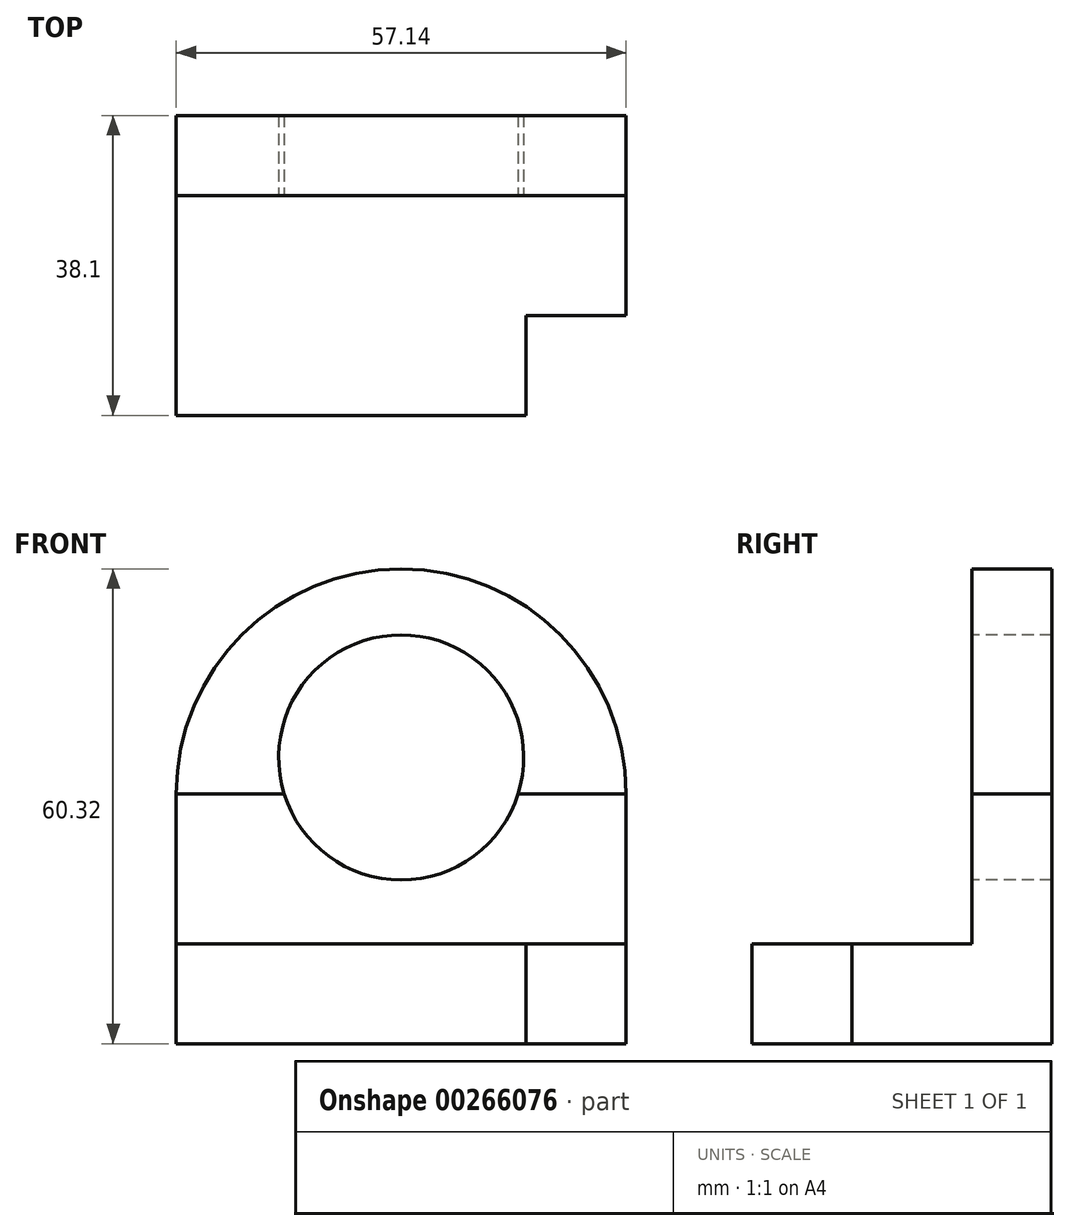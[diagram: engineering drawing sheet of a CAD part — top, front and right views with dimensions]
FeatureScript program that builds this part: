
annotation { "Feature Type Name" : "Feature", "Feature Type Description" : "" }
export const myFeature = defineFeature(function(context is Context, id is Id, definition is map)
    precondition{}
    {
        {
            var Q0;
            Q0=qCreatedBy(makeId("Top.planeOp"),FACE);
            var sketch = newSketch(context, id + "F0", { "sketchPlane" : qUnion([Q0])});
            skLineSegment(sketch, "E0.bottom", {"start": v(-28.57, 19.05) * mm, "end": v(28.58, 19.05) * mm});
            skLineSegment(sketch, "E0.top", {"start": v(-28.58, -19.05) * mm, "end": v(28.57, -19.05) * mm});
            skLineSegment(sketch, "E0.left", {"start": v(-28.57, 19.05) * mm, "end": v(-28.58, -19.05) * mm});
            skLineSegment(sketch, "E0.right", {"start": v(28.58, 19.05) * mm, "end": v(28.57, -19.05) * mm});
            skPoint(sketch, "E0.middle", {"position": v(0, 0) * mm});
            skSolve(sketch);
        }
        {
            var Q0;
            Q0 = qSketchRegion(id + "F0", true);
            extrude(context, id + "F1", {"entities" : qUnion([Q0]), "endBound" : BoundingType.SYMMETRIC, "depth" : 12.7 * mm});
        }
        {
            var Q0;
            Q0=qCreatedBy(makeId("Top.planeOp"),FACE);
            var sketch = newSketch(context, id + "F2", { "sketchPlane" : qUnion([Q0])});
            skLineSegment(sketch, "E1.bottom", {"start": v(28.57, -6.35) * mm, "end": v(15.87, -6.35) * mm});
            skLineSegment(sketch, "E1.top", {"start": v(28.57, -19.05) * mm, "end": v(15.88, -19.05) * mm});
            skLineSegment(sketch, "E1.left", {"start": v(28.57, -6.35) * mm, "end": v(28.57, -19.05) * mm});
            skLineSegment(sketch, "E1.right", {"start": v(15.87, -6.35) * mm, "end": v(15.88, -19.05) * mm});
            skSolve(sketch);
        }
        {
            var Q0;
            Q0 = qSketchRegion(id + "F2", true);
            extrude(context, id + "F3", {"entities" : qUnion([Q0]), "operationType" : NewBodyOperationType.REMOVE, "endBound" : BoundingType.SYMMETRIC, "oppositeDirection" : true, "depth" : 12.7 * mm});
        }
        {
            var Q0;
            Q0=qCreatedBy(makeId("Top.planeOp"),FACE);
            var sketch = newSketch(context, id + "F4", { "sketchPlane" : qUnion([Q0])});
            skLineSegment(sketch, "E2.bottom", {"start": v(-28.57, 19.05) * mm, "end": v(28.58, 19.05) * mm});
            skLineSegment(sketch, "E2.top", {"start": v(-28.57, 8.89) * mm, "end": v(28.58, 8.89) * mm});
            skLineSegment(sketch, "E2.left", {"start": v(-28.57, 19.05) * mm, "end": v(-28.57, 8.89) * mm});
            skLineSegment(sketch, "E2.right", {"start": v(28.58, 19.05) * mm, "end": v(28.58, 8.89) * mm});
            skSolve(sketch);
        }
        {
            var Q0;
            Q0 = qSketchRegion(id + "F4", true);
            extrude(context, id + "F5", {"entities" : qUnion([Q0]), "operationType" : NewBodyOperationType.ADD, "depth" : 25.4 * mm});
        }
        {
            var Q0;
            Q0=makeQuery(id+"F5.boolean.opBoolean","MERGE",FACE,{"derivedFrom":[makeQuery(id+"F1.opExtrude","SWEPT_FACE",FACE,{"disambiguationData":[OSD([sQuery(id+"F0.wireOp",EDGE,"E0.bottom")])]}),makeQuery(id+"F5.opExtrude","SWEPT_FACE",FACE,{"disambiguationData":[OSD([sQuery(id+"F4.wireOp",EDGE,"E2.bottom")])]})]});
            var sketch = newSketch(context, id + "F6", { "sketchPlane" : qUnion([Q0])});
            skCircle(sketch, "E3", {"center": v(0, 25.4) * mm, "radius": 28.57 * mm});
            skSolve(sketch);
        }
        {
            var Q0;
            {var subQ1=sQuery(id+"F4.wireOp",EDGE,"E2.bottom");var subQ3=makeQuery(id+"F5.opExtrude","CAP_EDGE",EDGE,{"disambiguationData":[OSD([subQ1])],"isStart":false});Q0=makeQuery(id+"F6.imprint","IMPRINT",FACE,{"disambiguationData":[TD([[makeQuery(id+"F6.imprint","IMPRINT",EDGE,{"derivedFrom":subQ3}),-1.0]])]});}
            var Q1;
            Q1=sQuery(id+"F6.wireOp",EDGE,"E3");
            extrude(context, id + "F7", {"entities" : qUnion([Q0]), "surfaceEntities" : qUnion([Q1]), "oppositeDirection" : true, "depth" : 10.16 * mm});
        }
        {
            var Q0;
            Q0=makeQuery(id+"F7.opExtrude","CAP_FACE",FACE,{"disambiguationData":[OSD([sQuery(id+"F4.wireOp",EDGE,"E2.bottom"),sQuery(id+"F6.wireOp",EDGE,"E3")])],"isStart":false});
            var sketch = newSketch(context, id + "F8", { "sketchPlane" : qUnion([Q0])});
            skCircle(sketch, "E4", {"center": v(0, 30) * mm, "radius": 15.57 * mm});
            skSolve(sketch);
        }
        {
            var Q0;
            {var subQ0=sQuery(id+"F8.wireOp",EDGE,"E4");var subQ1=makeQuery(id+"F7.opExtrude","CAP_EDGE",EDGE,{"disambiguationData":[OSD([sQuery(id+"F4.wireOp",EDGE,"E2.bottom")])],"isStart":false});var subQ2=makeQuery(id+"F8.imprint","INTERSECT",VERTEX,{"disambiguationData":[OD(0.0)],"derivedFrom":[subQ1,subQ0]});Q0=makeQuery(id+"F8.imprint","IMPRINT",FACE,{"disambiguationData":[TD([[makeQuery(id+"F8.imprint","IMPRINT",EDGE,{"disambiguationData":[TD([[subQ2,1.0]])],"derivedFrom":subQ0}),1.0]])]});}
            var Q1;
            {var subQ0=sQuery(id+"F8.wireOp",EDGE,"E4");var subQ1=makeQuery(id+"F7.opExtrude","CAP_EDGE",EDGE,{"disambiguationData":[OSD([sQuery(id+"F4.wireOp",EDGE,"E2.bottom")])],"isStart":false});var subQ2=makeQuery(id+"F8.imprint","INTERSECT",VERTEX,{"disambiguationData":[OD(0.0)],"derivedFrom":[subQ1,subQ0]});Q1=makeQuery(id+"F8.imprint","IMPRINT",FACE,{"disambiguationData":[TD([[makeQuery(id+"F8.imprint","IMPRINT",EDGE,{"disambiguationData":[TD([[subQ2,-1.0]])],"derivedFrom":subQ0}),1.0]])]});}
            extrude(context, id + "F9", {"entities" : qUnion([Q0, Q1]), "operationType" : NewBodyOperationType.REMOVE, "oppositeDirection" : true, "depth" : 10.16 * mm});
        }
    });
